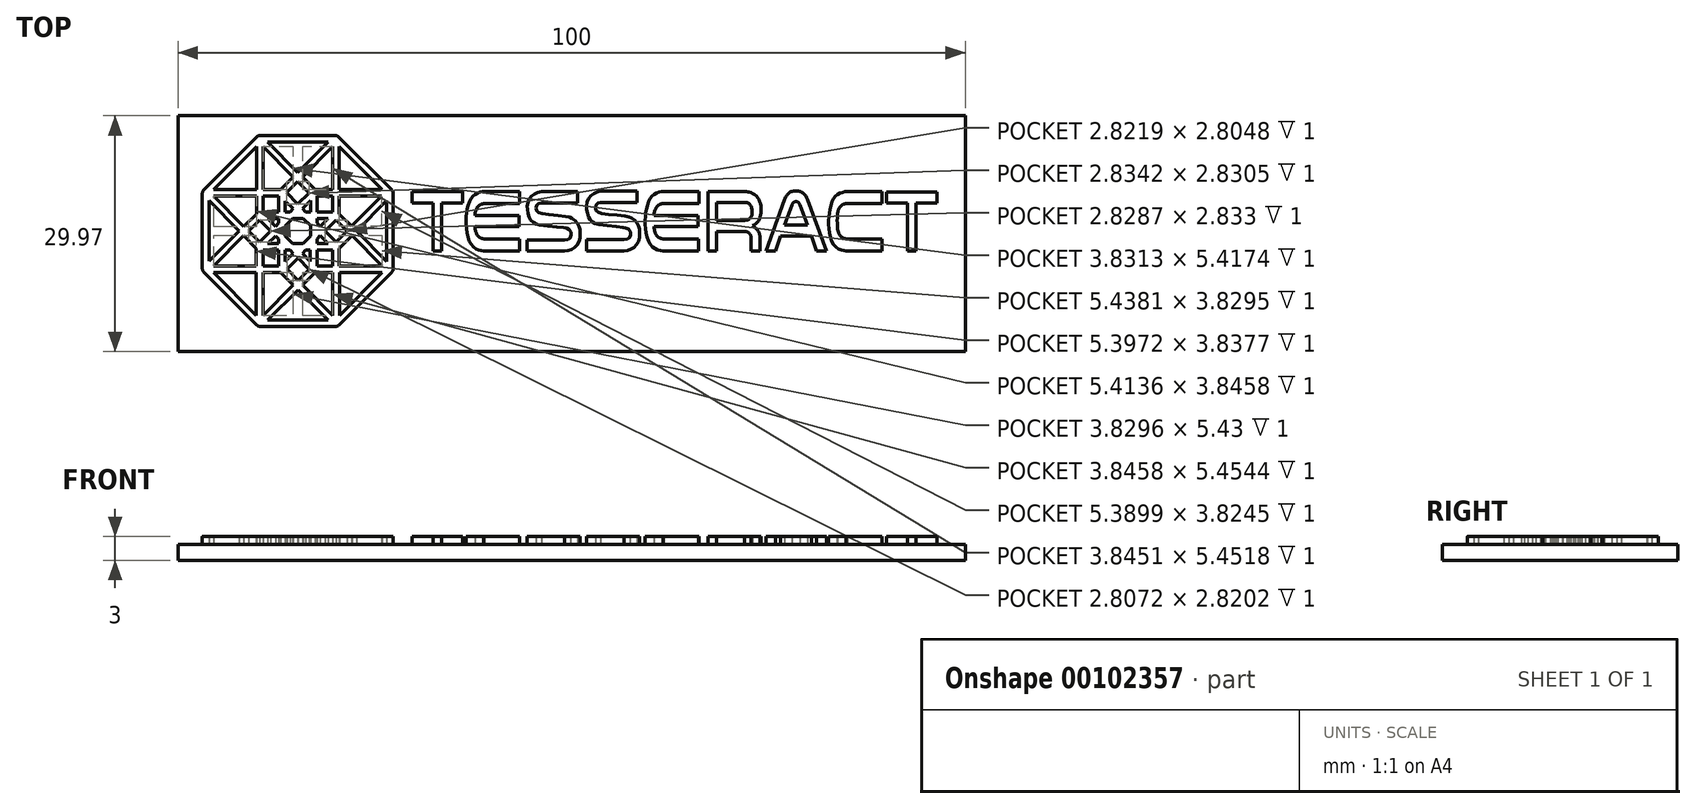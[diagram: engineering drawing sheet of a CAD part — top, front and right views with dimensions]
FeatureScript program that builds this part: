
annotation { "Feature Type Name" : "Feature", "Feature Type Description" : "" }
export const myFeature = defineFeature(function(context is Context, id is Id, definition is map)
    precondition{}
    {
        {
            var Q0;
            Q0=qCreatedBy(makeId("Top.planeOp"),FACE);
            var sketch = newSketch(context, id + "F0", { "sketchPlane" : qUnion([Q0])});
            skSolve(sketch);
        }
        {
            var Q0;
            Q0=qCreatedBy(makeId("Top.planeOp"),FACE);
            var sketch = newSketch(context, id + "F1", { "sketchPlane" : qUnion([Q0])});
            skLineSegment(sketch, "E0.bottom", {"start": v(-42.05, 24.86) * mm, "end": v(57.95, 24.86) * mm});
            skLineSegment(sketch, "E0.top", {"start": v(-42.05, -5.1) * mm, "end": v(57.95, -5.1) * mm});
            skLineSegment(sketch, "E0.left", {"start": v(-42.05, 24.86) * mm, "end": v(-42.05, -5.1) * mm});
            skLineSegment(sketch, "E0.right", {"start": v(57.95, 24.86) * mm, "end": v(57.95, -5.1) * mm});
            skSolve(sketch);
        }
        {
            var Q0;
            Q0=makeQuery(id+"F1.imprint","IMPRINT",FACE,{"disambiguationData":[TD([[makeQuery(id+"F1.imprint","IMPRINT",EDGE,{"derivedFrom":sQuery(id+"F1.wireOp",EDGE,"E0.bottom")}),-1.0]])]});
            extrude(context, id + "F2", {"entities" : qUnion([Q0]), "oppositeDirection" : true, "depth" : 2 * mm});
        }
        {
            var Q0;
            Q0=makeQuery(id+"F2.opExtrude","CAP_FACE",FACE,{"disambiguationData":[OSD([sQuery(id+"F1.wireOp",EDGE,"E0.bottom"),sQuery(id+"F1.wireOp",EDGE,"E0.top"),sQuery(id+"F1.wireOp",EDGE,"E0.left"),sQuery(id+"F1.wireOp",EDGE,"E0.right")])],"isStart":true});
            var sketch = newSketch(context, id + "F3", { "sketchPlane" : qUnion([Q0])});
            skLineSegment(sketch, "E1.bottom", {"start": v(-12.32, 15.2) * mm, "end": v(-5.94, 15.2) * mm});
            skLineSegment(sketch, "E1.top", {"start": v(-12.32, 13.79) * mm, "end": v(-9.67, 13.79) * mm});
            skLineSegment(sketch, "E1.left", {"start": v(-12.32, 15.2) * mm, "end": v(-12.32, 13.79) * mm});
            skLineSegment(sketch, "E1.right", {"start": v(-5.94, 15.2) * mm, "end": v(-5.94, 13.79) * mm});
            skLineSegment(sketch, "E2.bottom", {"start": v(-9.67, 7.67) * mm, "end": v(-8.58, 7.67) * mm});
            skLineSegment(sketch, "E2.left", {"start": v(-9.67, 7.67) * mm, "end": v(-9.67, 13.79) * mm});
            skLineSegment(sketch, "E2.right", {"start": v(-8.58, 7.67) * mm, "end": v(-8.58, 13.79) * mm});
            skLineSegment(sketch, "E3.trimOffspring", {"start": v(-8.58, 13.79) * mm, "end": v(-5.94, 13.79) * mm});
            skLineSegment(sketch, "E4.bottom", {"start": v(1.34, 13.7) * mm, "end": v(-3.1, 13.7) * mm});
            skLineSegment(sketch, "E4.top", {"start": v(1.34, 15.22) * mm, "end": v(-3.1, 15.22) * mm});
            skLineSegment(sketch, "E4.left", {"start": v(1.34, 13.7) * mm, "end": v(1.34, 15.22) * mm});
            skLineSegment(sketch, "E5.bottom", {"start": v(1.23, 12.16) * mm, "end": v(-4.36, 12.16) * mm});
            skLineSegment(sketch, "E5.top", {"start": v(1.23, 10.75) * mm, "end": v(-4.36, 10.75) * mm});
            skLineSegment(sketch, "E5.left", {"start": v(1.23, 12.16) * mm, "end": v(1.23, 10.75) * mm});
            skLineSegment(sketch, "E6.bottom", {"start": v(1.32, 9.22) * mm, "end": v(-3.23, 9.22) * mm});
            skLineSegment(sketch, "E6.top", {"start": v(1.32, 7.67) * mm, "end": v(-3.23, 7.67) * mm});
            skLineSegment(sketch, "E6.left", {"start": v(1.32, 9.22) * mm, "end": v(1.32, 7.67) * mm});
            skFitSpline(sketch, "E7", {"points": [v(-3.23, 9.22) * mm, v(-3.64, 9.32) * mm, v(-4.1, 9.77) * mm, v(-4.36, 10.75) * mm, v(-4.36, 12.16) * mm, v(-4.2, 12.95) * mm, v(-3.83, 13.45) * mm, v(-3.1, 13.7) * mm], "startDerivative": vector(-3.91, 0.56) * mm, "endDerivative": vector(8.28, 0.62) * mm});
            skFitSpline(sketch, "E8", {"points": [v(-3.23, 7.67) * mm, v(-3.9, 7.8) * mm, v(-4.7, 8.36) * mm, v(-5.31, 9.73) * mm, v(-5.48, 11.49) * mm, v(-5.35, 12.85) * mm, v(-4.89, 14.25) * mm, v(-4.33, 14.85) * mm, v(-3.68, 15.16) * mm, v(-3.1, 15.22) * mm], "startDerivative": vector(-7.35, 0.76) * mm, "endDerivative": vector(6.93, 0.14) * mm});
            skLineSegment(sketch, "E9.bottom", {"start": v(8.7, 13.79) * mm, "end": v(4.1, 13.79) * mm});
            skLineSegment(sketch, "E9.top", {"start": v(8.7, 15.22) * mm, "end": v(4.1, 15.22) * mm});
            skLineSegment(sketch, "E9.left", {"start": v(8.7, 13.79) * mm, "end": v(8.7, 15.22) * mm});
            skLineSegment(sketch, "E10.bottom", {"start": v(2.27, 7.65) * mm, "end": v(7.07, 7.65) * mm});
            skLineSegment(sketch, "E10.top", {"start": v(2.27, 9.08) * mm, "end": v(7.07, 9.08) * mm});
            skLineSegment(sketch, "E10.left", {"start": v(2.27, 7.65) * mm, "end": v(2.27, 9.08) * mm});
            skFitSpline(sketch, "E11", {"points": [v(7.07, 9.08) * mm, v(7.53, 9.18) * mm, v(7.81, 9.41) * mm, v(7.87, 9.86) * mm, v(7.75, 10.29) * mm, v(7.27, 10.57) * mm, v(6.93, 10.63) * mm, v(3.75, 11) * mm, v(3.25, 11.18) * mm, v(2.8, 11.54) * mm, v(2.49, 12.03) * mm, v(2.32, 12.78) * mm, v(2.3, 13.41) * mm, v(2.47, 14.12) * mm, v(2.86, 14.68) * mm, v(3.43, 15.05) * mm, v(4.1, 15.22) * mm], "startDerivative": vector(9.28, 1.26) * mm, "endDerivative": vector(10.61, 2.02) * mm});
            skFitSpline(sketch, "E12", {"points": [v(7.07, 7.65) * mm, v(7.67, 7.76) * mm, v(8.33, 8.09) * mm, v(8.79, 8.66) * mm, v(9, 9.43) * mm, v(8.98, 10.38) * mm, v(8.85, 10.93) * mm, v(8.44, 11.5) * mm, v(7.9, 11.87) * mm, v(7.39, 12.03) * mm, v(4.2, 12.4) * mm, v(3.62, 12.63) * mm, v(3.45, 12.93) * mm, v(3.44, 13.32) * mm, v(3.63, 13.65) * mm, v(4.1, 13.79) * mm], "startDerivative": vector(9.62, 1.1) * mm, "endDerivative": vector(9.31, 1.4) * mm});
            skLineSegment(sketch, "E13.bottom", {"start": v(16.24, 13.83) * mm, "end": v(11.64, 13.83) * mm});
            skLineSegment(sketch, "E13.top", {"start": v(16.24, 15.26) * mm, "end": v(11.64, 15.26) * mm});
            skLineSegment(sketch, "E13.left", {"start": v(16.24, 13.83) * mm, "end": v(16.24, 15.26) * mm});
            skLineSegment(sketch, "E14.bottom", {"start": v(9.82, 7.7) * mm, "end": v(14.62, 7.7) * mm});
            skLineSegment(sketch, "E14.top", {"start": v(9.82, 9.13) * mm, "end": v(14.62, 9.13) * mm});
            skLineSegment(sketch, "E14.left", {"start": v(9.82, 7.7) * mm, "end": v(9.82, 9.13) * mm});
            skFitSpline(sketch, "E15", {"points": [v(14.62, 9.13) * mm, v(15.08, 9.23) * mm, v(15.36, 9.46) * mm, v(15.43, 9.9) * mm, v(15.3, 10.33) * mm, v(14.82, 10.61) * mm, v(14.48, 10.68) * mm, v(11.3, 11.04) * mm, v(10.8, 11.22) * mm, v(10.34, 11.58) * mm, v(10.04, 12.07) * mm, v(9.87, 12.83) * mm, v(9.85, 13.46) * mm, v(10.02, 14.17) * mm, v(10.4, 14.72) * mm, v(10.98, 15.1) * mm, v(11.64, 15.26) * mm], "startDerivative": vector(9.28, 1.26) * mm, "endDerivative": vector(10.61, 2.02) * mm});
            skFitSpline(sketch, "E16", {"points": [v(14.62, 7.7) * mm, v(15.22, 7.8) * mm, v(15.88, 8.14) * mm, v(16.34, 8.7) * mm, v(16.55, 9.48) * mm, v(16.53, 10.43) * mm, v(16.4, 10.97) * mm, v(15.99, 11.54) * mm, v(15.45, 11.91) * mm, v(14.94, 12.07) * mm, v(11.75, 12.45) * mm, v(11.17, 12.67) * mm, v(11, 12.98) * mm, v(11, 13.37) * mm, v(11.18, 13.7) * mm, v(11.64, 13.83) * mm], "startDerivative": vector(9.62, 1.1) * mm, "endDerivative": vector(9.31, 1.4) * mm});
            skLineSegment(sketch, "E17.bottom", {"start": v(24.09, 13.7) * mm, "end": v(19.65, 13.7) * mm});
            skLineSegment(sketch, "E17.top", {"start": v(24.09, 15.22) * mm, "end": v(19.65, 15.22) * mm});
            skLineSegment(sketch, "E17.left", {"start": v(24.09, 13.7) * mm, "end": v(24.09, 15.22) * mm});
            skLineSegment(sketch, "E18.bottom", {"start": v(23.98, 12.17) * mm, "end": v(18.4, 12.17) * mm});
            skLineSegment(sketch, "E18.top", {"start": v(23.98, 10.76) * mm, "end": v(18.4, 10.76) * mm});
            skLineSegment(sketch, "E18.left", {"start": v(23.98, 12.17) * mm, "end": v(23.98, 10.76) * mm});
            skLineSegment(sketch, "E19.bottom", {"start": v(24.07, 9.2) * mm, "end": v(19.53, 9.2) * mm});
            skLineSegment(sketch, "E19.top", {"start": v(24.07, 7.68) * mm, "end": v(19.53, 7.68) * mm});
            skLineSegment(sketch, "E19.left", {"start": v(24.07, 9.2) * mm, "end": v(24.07, 7.68) * mm});
            skFitSpline(sketch, "E20", {"points": [v(19.53, 9.2) * mm, v(19.12, 9.33) * mm, v(18.66, 9.78) * mm, v(18.4, 10.76) * mm, v(18.4, 12.17) * mm, v(18.56, 12.95) * mm, v(18.92, 13.45) * mm, v(19.65, 13.7) * mm], "startDerivative": vector(-3.91, 0.56) * mm, "endDerivative": vector(8.28, 0.62) * mm});
            skFitSpline(sketch, "E21", {"points": [v(19.53, 7.68) * mm, v(18.86, 7.8) * mm, v(18.05, 8.37) * mm, v(17.44, 9.73) * mm, v(17.28, 11.5) * mm, v(17.4, 12.85) * mm, v(17.86, 14.25) * mm, v(18.42, 14.85) * mm, v(19.08, 15.16) * mm, v(19.65, 15.22) * mm], "startDerivative": vector(-7.35, 0.76) * mm, "endDerivative": vector(6.93, 0.14) * mm});
            skLineSegment(sketch, "E22.bottom", {"start": v(47.93, 15.2) * mm, "end": v(54.31, 15.2) * mm});
            skLineSegment(sketch, "E22.top", {"start": v(47.93, 13.78) * mm, "end": v(50.58, 13.78) * mm});
            skLineSegment(sketch, "E22.left", {"start": v(47.93, 15.2) * mm, "end": v(47.93, 13.78) * mm});
            skLineSegment(sketch, "E22.right", {"start": v(54.31, 15.2) * mm, "end": v(54.31, 13.78) * mm});
            skLineSegment(sketch, "E23.bottom", {"start": v(50.58, 7.66) * mm, "end": v(51.67, 7.66) * mm});
            skLineSegment(sketch, "E23.left", {"start": v(50.58, 7.66) * mm, "end": v(50.58, 13.78) * mm});
            skLineSegment(sketch, "E23.right", {"start": v(51.67, 7.66) * mm, "end": v(51.67, 13.78) * mm});
            skLineSegment(sketch, "E24.trimOffspring", {"start": v(51.67, 13.78) * mm, "end": v(54.31, 13.78) * mm});
            skLineSegment(sketch, "E25.bottom", {"start": v(25.25, 7.67) * mm, "end": v(26.37, 7.67) * mm});
            skLineSegment(sketch, "E25.top", {"start": v(25.25, 15.22) * mm, "end": v(26.37, 15.22) * mm});
            skLineSegment(sketch, "E25.left", {"start": v(25.25, 7.67) * mm, "end": v(25.25, 15.22) * mm});
            skLineSegment(sketch, "E25.right", {"start": v(26.37, 7.67) * mm, "end": v(26.37, 10.15) * mm});
            skLineSegment(sketch, "E26.bottom", {"start": v(26.37, 11.57) * mm, "end": v(29.9, 11.57) * mm});
            skLineSegment(sketch, "E26.top", {"start": v(26.37, 10.15) * mm, "end": v(29.9, 10.15) * mm});
            skLineSegment(sketch, "E27.bottom", {"start": v(26.37, 15.22) * mm, "end": v(29.95, 15.22) * mm});
            skLineSegment(sketch, "E27.top", {"start": v(26.37, 13.83) * mm, "end": v(29.95, 13.83) * mm});
            skLineSegment(sketch, "E28.trimOffspring", {"start": v(26.37, 11.57) * mm, "end": v(26.37, 13.83) * mm});
            skFitSpline(sketch, "E29", {"points": [v(29.95, 13.83) * mm, v(30.39, 13.74) * mm, v(30.69, 13.42) * mm, v(30.87, 12.72) * mm, v(30.71, 12) * mm, v(30.37, 11.65) * mm, v(29.9, 11.57) * mm], "startDerivative": vector(3.1, -0.3) * mm, "endDerivative": vector(-3.16, -0.18) * mm});
            skFitSpline(sketch, "E30", {"points": [v(30.93, 10.88) * mm, v(31.31, 11.1) * mm, v(31.7, 11.56) * mm, v(31.94, 12.2) * mm, v(32, 12.98) * mm, v(31.9, 13.75) * mm, v(31.62, 14.38) * mm, v(31.1, 14.9) * mm, v(30.56, 15.13) * mm, v(30.3, 15.2) * mm, v(29.95, 15.22) * mm], "startDerivative": vector(4.45, 2.16) * mm, "endDerivative": vector(-4.85, 0.22) * mm});
            skLineSegment(sketch, "E31.bottom", {"start": v(30.73, 7.68) * mm, "end": v(31.87, 7.68) * mm});
            skLineSegment(sketch, "E31.left", {"start": v(30.73, 7.68) * mm, "end": v(30.73, 9.36) * mm});
            skLineSegment(sketch, "E31.right", {"start": v(31.87, 7.68) * mm, "end": v(31.87, 9.36) * mm});
            skFitSpline(sketch, "E32", {"points": [v(29.9, 10.15) * mm, v(30.22, 10.1) * mm, v(30.45, 9.96) * mm, v(30.63, 9.74) * mm, v(30.7, 9.55) * mm, v(30.73, 9.36) * mm], "startDerivative": vector(1.5, -0.05) * mm, "endDerivative": vector(0.26, -0.85) * mm});
            skFitSpline(sketch, "E33", {"points": [v(30.93, 10.88) * mm, v(31.14, 10.77) * mm, v(31.37, 10.57) * mm, v(31.63, 10.22) * mm, v(31.77, 9.87) * mm, v(31.84, 9.64) * mm, v(31.87, 9.47) * mm, v(31.87, 9.36) * mm], "startDerivative": vector(1.44, -0.68) * mm, "endDerivative": vector(0.02, -1.5) * mm});
            skLineSegment(sketch, "E34", {"start": v(32.62, 7.67) * mm, "end": v(33.8, 7.67) * mm});
            skLineSegment(sketch, "E35", {"start": v(33.8, 7.67) * mm, "end": v(34.48, 9.55) * mm});
            skLineSegment(sketch, "E36", {"start": v(34.48, 9.55) * mm, "end": v(38.4, 9.55) * mm});
            skLineSegment(sketch, "E37", {"start": v(38.4, 9.55) * mm, "end": v(39.06, 7.67) * mm});
            skLineSegment(sketch, "E38", {"start": v(39.06, 7.67) * mm, "end": v(40.3, 7.67) * mm});
            skLineSegment(sketch, "E39", {"start": v(40.3, 7.67) * mm, "end": v(37.91, 14.2) * mm});
            skLineSegment(sketch, "E40", {"start": v(34.97, 14.2) * mm, "end": v(32.62, 7.67) * mm});
            skLineSegment(sketch, "E41", {"start": v(34.98, 10.95) * mm, "end": v(37.88, 10.95) * mm});
            skLineSegment(sketch, "E42", {"start": v(37.88, 10.95) * mm, "end": v(36.95, 13.5) * mm});
            skLineSegment(sketch, "E43", {"start": v(35.9, 13.5) * mm, "end": v(34.98, 10.95) * mm});
            skFitSpline(sketch, "E44", {"points": [v(35.9, 13.5) * mm, v(36.06, 13.77) * mm, v(36.26, 13.91) * mm, v(36.43, 13.94) * mm, v(36.66, 13.9) * mm, v(36.84, 13.7) * mm, v(36.95, 13.5) * mm], "startDerivative": vector(0.68, 1.52) * mm, "endDerivative": vector(0.61, -1.19) * mm});
            skFitSpline(sketch, "E45", {"points": [v(34.97, 14.2) * mm, v(35.24, 14.68) * mm, v(35.63, 15.1) * mm, v(35.99, 15.27) * mm, v(36.83, 15.28) * mm, v(37.3, 15.06) * mm, v(37.66, 14.65) * mm, v(37.91, 14.2) * mm], "startDerivative": vector(1.68, 3.45) * mm, "endDerivative": vector(1.65, -3.33) * mm});
            skLineSegment(sketch, "E46.bottom", {"start": v(47.38, 13.72) * mm, "end": v(42.95, 13.72) * mm});
            skLineSegment(sketch, "E46.top", {"start": v(47.38, 15.23) * mm, "end": v(42.97, 15.23) * mm});
            skLineSegment(sketch, "E46.left", {"start": v(47.38, 13.72) * mm, "end": v(47.38, 15.23) * mm});
            skLineSegment(sketch, "E47.bottom", {"start": v(47.36, 9.21) * mm, "end": v(42.82, 9.21) * mm});
            skLineSegment(sketch, "E47.top", {"start": v(47.36, 7.68) * mm, "end": v(42.81, 7.68) * mm});
            skLineSegment(sketch, "E47.left", {"start": v(47.36, 9.21) * mm, "end": v(47.36, 7.68) * mm});
            skFitSpline(sketch, "E48", {"points": [v(42.82, 9.21) * mm, v(42.41, 9.34) * mm, v(41.95, 9.79) * mm, v(41.69, 10.77) * mm, v(41.69, 12.18) * mm, v(41.85, 12.96) * mm, v(42.22, 13.46) * mm, v(42.95, 13.72) * mm], "startDerivative": vector(-3.91, 0.56) * mm, "endDerivative": vector(8.28, 0.62) * mm});
            skFitSpline(sketch, "E49", {"points": [v(42.81, 7.68) * mm, v(42.21, 7.8) * mm, v(41.36, 8.3) * mm, v(40.75, 9.67) * mm, v(40.59, 11.43) * mm, v(40.71, 12.79) * mm, v(41.13, 14.2) * mm, v(41.72, 14.84) * mm, v(42.35, 15.13) * mm, v(42.97, 15.23) * mm], "startDerivative": vector(-7.35, 0.76) * mm, "endDerivative": vector(6.93, 0.14) * mm});
            skFitSpline(sketch, "E50", {"points": [v(41.69, 10.77) * mm, v(41.67, 11.4) * mm, v(41.69, 12.18) * mm], "startDerivative": vector(-0.09, 1.41) * mm, "endDerivative": vector(0.09, 1.4) * mm});
            skLineSegment(sketch, "E51", {"start": v(-28.45, 9.55) * mm, "end": v(-27.5, 8.62) * mm});
            skLineSegment(sketch, "E52", {"start": v(-27.5, 8.62) * mm, "end": v(-26.2, 8.62) * mm});
            skLineSegment(sketch, "E53", {"start": v(-26.2, 8.62) * mm, "end": v(-25.25, 9.54) * mm});
            skLineSegment(sketch, "E54", {"start": v(-25.25, 9.54) * mm, "end": v(-25.25, 10.88) * mm});
            skLineSegment(sketch, "E55", {"start": v(-25.25, 10.88) * mm, "end": v(-26.17, 11.81) * mm});
            skLineSegment(sketch, "E56", {"start": v(-26.17, 11.81) * mm, "end": v(-27.48, 11.81) * mm});
            skLineSegment(sketch, "E57", {"start": v(-27.48, 11.81) * mm, "end": v(-28.44, 10.87) * mm});
            skLineSegment(sketch, "E58", {"start": v(-28.44, 10.87) * mm, "end": v(-28.45, 9.55) * mm});
            skLineSegment(sketch, "E59", {"start": v(-24.42, 11.21) * mm, "end": v(-24.42, 11.8) * mm});
            skLineSegment(sketch, "E60", {"start": v(-24.42, 11.8) * mm, "end": v(-23.01, 11.8) * mm});
            skLineSegment(sketch, "E61", {"start": v(-23.01, 11.8) * mm, "end": v(-24, 10.8) * mm});
            skLineSegment(sketch, "E62", {"start": v(-24, 10.8) * mm, "end": v(-24.42, 11.21) * mm});
            skLineSegment(sketch, "E63", {"start": v(-24.43, 9.21) * mm, "end": v(-24.43, 8.62) * mm});
            skLineSegment(sketch, "E64", {"start": v(-24.43, 8.62) * mm, "end": v(-23.01, 8.62) * mm});
            skLineSegment(sketch, "E65", {"start": v(-23.01, 8.62) * mm, "end": v(-24, 9.62) * mm});
            skLineSegment(sketch, "E66", {"start": v(-24, 9.62) * mm, "end": v(-24.43, 9.21) * mm});
            skLineSegment(sketch, "E67", {"start": v(-23.4, 10.23) * mm, "end": v(-21.98, 8.8) * mm});
            skLineSegment(sketch, "E68", {"start": v(-21.98, 8.8) * mm, "end": v(-20.58, 10.2) * mm});
            skLineSegment(sketch, "E69", {"start": v(-20.58, 10.2) * mm, "end": v(-21.99, 11.6) * mm});
            skLineSegment(sketch, "E70", {"start": v(-21.99, 11.6) * mm, "end": v(-23.4, 10.23) * mm});
            skLineSegment(sketch, "E71", {"start": v(-28.44, 12.63) * mm, "end": v(-27.85, 12.63) * mm});
            skLineSegment(sketch, "E72", {"start": v(-27.85, 12.63) * mm, "end": v(-27.44, 13.05) * mm});
            skLineSegment(sketch, "E73", {"start": v(-27.44, 13.05) * mm, "end": v(-28.44, 14.03) * mm});
            skLineSegment(sketch, "E74", {"start": v(-28.44, 14.03) * mm, "end": v(-28.44, 12.63) * mm});
            skLineSegment(sketch, "E75", {"start": v(-25.84, 12.63) * mm, "end": v(-25.24, 12.63) * mm});
            skLineSegment(sketch, "E76", {"start": v(-25.24, 12.63) * mm, "end": v(-25.24, 14.06) * mm});
            skLineSegment(sketch, "E77", {"start": v(-25.24, 14.06) * mm, "end": v(-26.25, 13.06) * mm});
            skLineSegment(sketch, "E78", {"start": v(-26.25, 13.06) * mm, "end": v(-25.84, 12.63) * mm});
            skLineSegment(sketch, "E79", {"start": v(-28.27, 15.08) * mm, "end": v(-26.85, 13.65) * mm});
            skLineSegment(sketch, "E80", {"start": v(-26.85, 13.65) * mm, "end": v(-25.43, 15.06) * mm});
            skLineSegment(sketch, "E81", {"start": v(-25.43, 15.06) * mm, "end": v(-26.85, 16.48) * mm});
            skLineSegment(sketch, "E82", {"start": v(-26.85, 16.48) * mm, "end": v(-28.27, 15.08) * mm});
            skLineSegment(sketch, "E83", {"start": v(-30.68, 8.62) * mm, "end": v(-29.27, 8.62) * mm});
            skLineSegment(sketch, "E84", {"start": v(-29.27, 8.62) * mm, "end": v(-29.27, 9.2) * mm});
            skLineSegment(sketch, "E85", {"start": v(-29.27, 9.2) * mm, "end": v(-29.68, 9.6) * mm});
            skLineSegment(sketch, "E86", {"start": v(-29.68, 9.6) * mm, "end": v(-30.68, 8.62) * mm});
            skLineSegment(sketch, "E87", {"start": v(-30.67, 11.8) * mm, "end": v(-29.29, 11.8) * mm});
            skLineSegment(sketch, "E88", {"start": v(-29.29, 11.8) * mm, "end": v(-29.29, 11.2) * mm});
            skLineSegment(sketch, "E89", {"start": v(-29.29, 11.2) * mm, "end": v(-29.67, 10.8) * mm});
            skLineSegment(sketch, "E90", {"start": v(-29.67, 10.8) * mm, "end": v(-30.67, 11.8) * mm});
            skLineSegment(sketch, "E91", {"start": v(-33.1, 10.21) * mm, "end": v(-31.7, 8.79) * mm});
            skLineSegment(sketch, "E92", {"start": v(-31.7, 8.79) * mm, "end": v(-30.28, 10.2) * mm});
            skLineSegment(sketch, "E93", {"start": v(-30.28, 10.2) * mm, "end": v(-31.69, 11.62) * mm});
            skLineSegment(sketch, "E94", {"start": v(-31.69, 11.62) * mm, "end": v(-33.1, 10.21) * mm});
            skLineSegment(sketch, "E95", {"start": v(-28.44, 6.35) * mm, "end": v(-28.44, 7.79) * mm});
            skLineSegment(sketch, "E96", {"start": v(-28.44, 7.79) * mm, "end": v(-27.85, 7.79) * mm});
            skLineSegment(sketch, "E97", {"start": v(-27.85, 7.79) * mm, "end": v(-27.45, 7.36) * mm});
            skLineSegment(sketch, "E98", {"start": v(-27.45, 7.36) * mm, "end": v(-28.44, 6.35) * mm});
            skLineSegment(sketch, "E99", {"start": v(-25.84, 7.77) * mm, "end": v(-25.26, 7.77) * mm});
            skLineSegment(sketch, "E100", {"start": v(-25.26, 7.77) * mm, "end": v(-25.26, 6.36) * mm});
            skLineSegment(sketch, "E101", {"start": v(-25.26, 6.36) * mm, "end": v(-26.25, 7.36) * mm});
            skLineSegment(sketch, "E102", {"start": v(-26.25, 7.36) * mm, "end": v(-25.84, 7.77) * mm});
            skLineSegment(sketch, "E103", {"start": v(-26.84, 6.77) * mm, "end": v(-25.43, 5.34) * mm});
            skLineSegment(sketch, "E104", {"start": v(-25.43, 5.34) * mm, "end": v(-26.84, 3.95) * mm});
            skLineSegment(sketch, "E105", {"start": v(-26.84, 3.95) * mm, "end": v(-28.24, 5.36) * mm});
            skLineSegment(sketch, "E106", {"start": v(-28.24, 5.36) * mm, "end": v(-26.84, 6.77) * mm});
            skLineSegment(sketch, "E107.bottom", {"start": v(-31.28, 7.77) * mm, "end": v(-29.26, 7.77) * mm});
            skLineSegment(sketch, "E107.top", {"start": v(-31.28, 5.75) * mm, "end": v(-29.26, 5.75) * mm});
            skLineSegment(sketch, "E107.left", {"start": v(-31.28, 7.77) * mm, "end": v(-31.28, 5.75) * mm});
            skLineSegment(sketch, "E107.right", {"start": v(-29.26, 7.77) * mm, "end": v(-29.26, 5.75) * mm});
            skLineSegment(sketch, "E108.bottom", {"start": v(-24.42, 7.78) * mm, "end": v(-22.4, 7.78) * mm});
            skLineSegment(sketch, "E108.top", {"start": v(-24.42, 5.76) * mm, "end": v(-22.4, 5.76) * mm});
            skLineSegment(sketch, "E108.left", {"start": v(-24.42, 7.78) * mm, "end": v(-24.42, 5.76) * mm});
            skLineSegment(sketch, "E108.right", {"start": v(-22.4, 7.78) * mm, "end": v(-22.4, 5.76) * mm});
            skLineSegment(sketch, "E109.bottom", {"start": v(-31.28, 14.64) * mm, "end": v(-29.26, 14.64) * mm});
            skLineSegment(sketch, "E109.top", {"start": v(-31.28, 12.62) * mm, "end": v(-29.26, 12.62) * mm});
            skLineSegment(sketch, "E109.left", {"start": v(-31.28, 14.64) * mm, "end": v(-31.28, 12.62) * mm});
            skLineSegment(sketch, "E109.right", {"start": v(-29.26, 14.64) * mm, "end": v(-29.26, 12.62) * mm});
            skLineSegment(sketch, "E110.bottom", {"start": v(-24.42, 14.64) * mm, "end": v(-22.4, 14.64) * mm});
            skLineSegment(sketch, "E110.top", {"start": v(-24.42, 12.62) * mm, "end": v(-22.4, 12.62) * mm});
            skLineSegment(sketch, "E110.left", {"start": v(-24.42, 14.64) * mm, "end": v(-24.42, 12.62) * mm});
            skLineSegment(sketch, "E110.right", {"start": v(-22.4, 14.64) * mm, "end": v(-22.4, 12.62) * mm});
            skLineSegment(sketch, "E111", {"start": v(-37.55, 15.47) * mm, "end": v(-32.1, 15.47) * mm});
            skLineSegment(sketch, "E112", {"start": v(-32.1, 15.47) * mm, "end": v(-32.1, 20.92) * mm});
            skLineSegment(sketch, "E113", {"start": v(-32.1, 20.92) * mm, "end": v(-37.55, 15.47) * mm});
            skLineSegment(sketch, "E114", {"start": v(-31.29, 20.92) * mm, "end": v(-31.29, 15.5) * mm});
            skLineSegment(sketch, "E115", {"start": v(-31.29, 15.5) * mm, "end": v(-29.05, 15.5) * mm});
            skLineSegment(sketch, "E116", {"start": v(-29.05, 15.5) * mm, "end": v(-27.45, 17.09) * mm});
            skLineSegment(sketch, "E117", {"start": v(-27.45, 17.09) * mm, "end": v(-31.29, 20.92) * mm});
            skLineSegment(sketch, "E118", {"start": v(-30.68, 21.54) * mm, "end": v(-23.02, 21.54) * mm});
            skLineSegment(sketch, "E119", {"start": v(-23.02, 21.54) * mm, "end": v(-26.84, 17.66) * mm});
            skLineSegment(sketch, "E120", {"start": v(-26.84, 17.66) * mm, "end": v(-30.68, 21.54) * mm});
            skLineSegment(sketch, "E121", {"start": v(-22.4, 20.93) * mm, "end": v(-22.4, 15.47) * mm});
            skLineSegment(sketch, "E122", {"start": v(-22.4, 15.47) * mm, "end": v(-24.65, 15.47) * mm});
            skLineSegment(sketch, "E123", {"start": v(-24.65, 15.47) * mm, "end": v(-26.25, 17.07) * mm});
            skLineSegment(sketch, "E124", {"start": v(-26.25, 17.07) * mm, "end": v(-22.4, 20.93) * mm});
            skLineSegment(sketch, "E125", {"start": v(-21.58, 20.92) * mm, "end": v(-21.58, 15.49) * mm});
            skLineSegment(sketch, "E126", {"start": v(-21.58, 15.49) * mm, "end": v(-16.15, 15.49) * mm});
            skLineSegment(sketch, "E127", {"start": v(-16.15, 15.49) * mm, "end": v(-21.58, 20.92) * mm});
            skLineSegment(sketch, "E128", {"start": v(-21.58, 12.4) * mm, "end": v(-21.58, 14.64) * mm});
            skLineSegment(sketch, "E129", {"start": v(-21.58, 14.64) * mm, "end": v(-16.19, 14.64) * mm});
            skLineSegment(sketch, "E130", {"start": v(-16.19, 14.64) * mm, "end": v(-20, 10.81) * mm});
            skLineSegment(sketch, "E131", {"start": v(-20, 10.81) * mm, "end": v(-21.58, 12.4) * mm});
            skLineSegment(sketch, "E132", {"start": v(-15.54, 14.07) * mm, "end": v(-15.54, 6.34) * mm});
            skLineSegment(sketch, "E133", {"start": v(-15.54, 6.34) * mm, "end": v(-19.39, 10.21) * mm});
            skLineSegment(sketch, "E134", {"start": v(-19.39, 10.21) * mm, "end": v(-15.54, 14.07) * mm});
            skLineSegment(sketch, "E135", {"start": v(-21.58, 8) * mm, "end": v(-21.58, 5.79) * mm});
            skLineSegment(sketch, "E136", {"start": v(-21.58, 5.79) * mm, "end": v(-16.14, 5.79) * mm});
            skLineSegment(sketch, "E137", {"start": v(-16.14, 5.79) * mm, "end": v(-19.98, 9.62) * mm});
            skLineSegment(sketch, "E138", {"start": v(-19.98, 9.62) * mm, "end": v(-21.58, 8) * mm});
            skLineSegment(sketch, "E139", {"start": v(-21.57, -0.5) * mm, "end": v(-21.57, 4.93) * mm});
            skLineSegment(sketch, "E140", {"start": v(-21.57, 4.93) * mm, "end": v(-16.16, 4.93) * mm});
            skLineSegment(sketch, "E141", {"start": v(-16.16, 4.93) * mm, "end": v(-21.57, -0.5) * mm});
            skLineSegment(sketch, "E142", {"start": v(-24.66, 4.93) * mm, "end": v(-22.4, 4.93) * mm});
            skLineSegment(sketch, "E143", {"start": v(-22.4, 4.93) * mm, "end": v(-22.4, -0.52) * mm});
            skLineSegment(sketch, "E144", {"start": v(-22.4, -0.52) * mm, "end": v(-26.25, 3.34) * mm});
            skLineSegment(sketch, "E145", {"start": v(-26.25, 3.34) * mm, "end": v(-24.66, 4.93) * mm});
            skLineSegment(sketch, "E146", {"start": v(-30.68, -1.09) * mm, "end": v(-23, -1.09) * mm});
            skLineSegment(sketch, "E147", {"start": v(-23, -1.09) * mm, "end": v(-26.84, 2.74) * mm});
            skLineSegment(sketch, "E148", {"start": v(-26.84, 2.74) * mm, "end": v(-30.68, -1.09) * mm});
            skLineSegment(sketch, "E149", {"start": v(-31.28, -0.5) * mm, "end": v(-31.28, 4.93) * mm});
            skLineSegment(sketch, "E150", {"start": v(-31.28, 4.93) * mm, "end": v(-29.03, 4.93) * mm});
            skLineSegment(sketch, "E151", {"start": v(-29.03, 4.93) * mm, "end": v(-27.45, 3.35) * mm});
            skLineSegment(sketch, "E152", {"start": v(-27.45, 3.35) * mm, "end": v(-31.28, -0.5) * mm});
            skLineSegment(sketch, "E153", {"start": v(-32.12, -0.5) * mm, "end": v(-32.12, 4.93) * mm});
            skLineSegment(sketch, "E154", {"start": v(-32.12, 4.93) * mm, "end": v(-37.55, 4.93) * mm});
            skLineSegment(sketch, "E155", {"start": v(-37.55, 4.93) * mm, "end": v(-32.12, -0.5) * mm});
            skLineSegment(sketch, "E156", {"start": v(-37.53, 5.77) * mm, "end": v(-32.13, 5.77) * mm});
            skLineSegment(sketch, "E157", {"start": v(-32.13, 5.77) * mm, "end": v(-32.13, 8) * mm});
            skLineSegment(sketch, "E158", {"start": v(-32.13, 8) * mm, "end": v(-33.7, 9.61) * mm});
            skLineSegment(sketch, "E159", {"start": v(-33.7, 9.61) * mm, "end": v(-37.53, 5.77) * mm});
            skLineSegment(sketch, "E160", {"start": v(-38.14, 6.38) * mm, "end": v(-38.14, 14.06) * mm});
            skLineSegment(sketch, "E161", {"start": v(-38.14, 14.06) * mm, "end": v(-34.32, 10.21) * mm});
            skLineSegment(sketch, "E162", {"start": v(-34.32, 10.21) * mm, "end": v(-38.14, 6.38) * mm});
            skLineSegment(sketch, "E163", {"start": v(-37.52, 14.65) * mm, "end": v(-32.1, 14.65) * mm});
            skLineSegment(sketch, "E164", {"start": v(-32.1, 14.65) * mm, "end": v(-32.1, 12.4) * mm});
            skLineSegment(sketch, "E165", {"start": v(-32.1, 12.4) * mm, "end": v(-33.7, 10.8) * mm});
            skLineSegment(sketch, "E166", {"start": v(-37.52, 14.65) * mm, "end": v(-33.7, 10.8) * mm});
            skLineSegment(sketch, "E167", {"start": v(-38.97, 5.16) * mm, "end": v(-38.97, 15.27) * mm});
            skLineSegment(sketch, "E168", {"start": v(-31.9, -1.91) * mm, "end": v(-21.78, -1.91) * mm});
            skLineSegment(sketch, "E169", {"start": v(-14.73, 5.17) * mm, "end": v(-14.73, 15.27) * mm});
            skLineSegment(sketch, "E170", {"start": v(-21.84, 22.36) * mm, "end": v(-31.9, 22.36) * mm});
            skLineSegment(sketch, "E171", {"start": v(-38.97, 15.27) * mm, "end": v(-31.9, 22.36) * mm});
            skLineSegment(sketch, "E172", {"start": v(-21.84, 22.36) * mm, "end": v(-14.73, 15.27) * mm});
            skLineSegment(sketch, "E173", {"start": v(-21.78, -1.91) * mm, "end": v(-14.73, 5.17) * mm});
            skLineSegment(sketch, "E174", {"start": v(-38.97, 5.16) * mm, "end": v(-31.9, -1.91) * mm});
            skSolve(sketch);
        }
        {
            var Q0;
            Q0=qSketchRegion(id+"F3",true);
            extrude(context, id + "F4", {"entities" : qUnion([Q0]), "operationType" : NewBodyOperationType.ADD, "depth" : 1 * mm});
        }
        {
            var Q0;
            Q0=makeQuery(id+"F4.opExtrude","SWEPT_EDGE",EDGE,{"disambiguationData":[OSD([sQuery(id+"F3.wireOp",EDGE,"E169"),sQuery(id+"F3.wireOp",EDGE,"E172")])]});
            var Q1;
            Q1=makeQuery(id+"F4.opExtrude","SWEPT_EDGE",EDGE,{"disambiguationData":[OSD([sQuery(id+"F3.wireOp",EDGE,"E169"),sQuery(id+"F3.wireOp",EDGE,"E173")])]});
            var Q2;
            Q2=makeQuery(id+"F4.opExtrude","SWEPT_EDGE",EDGE,{"disambiguationData":[OSD([sQuery(id+"F3.wireOp",EDGE,"E168"),sQuery(id+"F3.wireOp",EDGE,"E173")])]});
            var Q3;
            Q3=makeQuery(id+"F4.opExtrude","SWEPT_EDGE",EDGE,{"disambiguationData":[OSD([sQuery(id+"F3.wireOp",EDGE,"E168"),sQuery(id+"F3.wireOp",EDGE,"E174")])]});
            var Q4;
            Q4=makeQuery(id+"F4.opExtrude","SWEPT_EDGE",EDGE,{"disambiguationData":[OSD([sQuery(id+"F3.wireOp",EDGE,"E167"),sQuery(id+"F3.wireOp",EDGE,"E174")])]});
            var Q5;
            Q5=makeQuery(id+"F4.opExtrude","SWEPT_EDGE",EDGE,{"disambiguationData":[OSD([sQuery(id+"F3.wireOp",EDGE,"E170"),sQuery(id+"F3.wireOp",EDGE,"E172")])]});
            var Q6;
            Q6=makeQuery(id+"F4.opExtrude","SWEPT_EDGE",EDGE,{"disambiguationData":[OSD([sQuery(id+"F3.wireOp",EDGE,"E170"),sQuery(id+"F3.wireOp",EDGE,"E171")])]});
            var Q7;
            Q7=makeQuery(id+"F4.opExtrude","SWEPT_EDGE",EDGE,{"disambiguationData":[OSD([sQuery(id+"F3.wireOp",EDGE,"E167"),sQuery(id+"F3.wireOp",EDGE,"E171")])]});
            fillet(context, id + "F5", {"entities" : qUnion([Q0, Q1, Q2, Q3, Q4, Q5, Q6, Q7]), "radius" : 0.7 * mm, "tangentPropagation" : true, "allowEdgeOverflow" : false});
        }
    });
